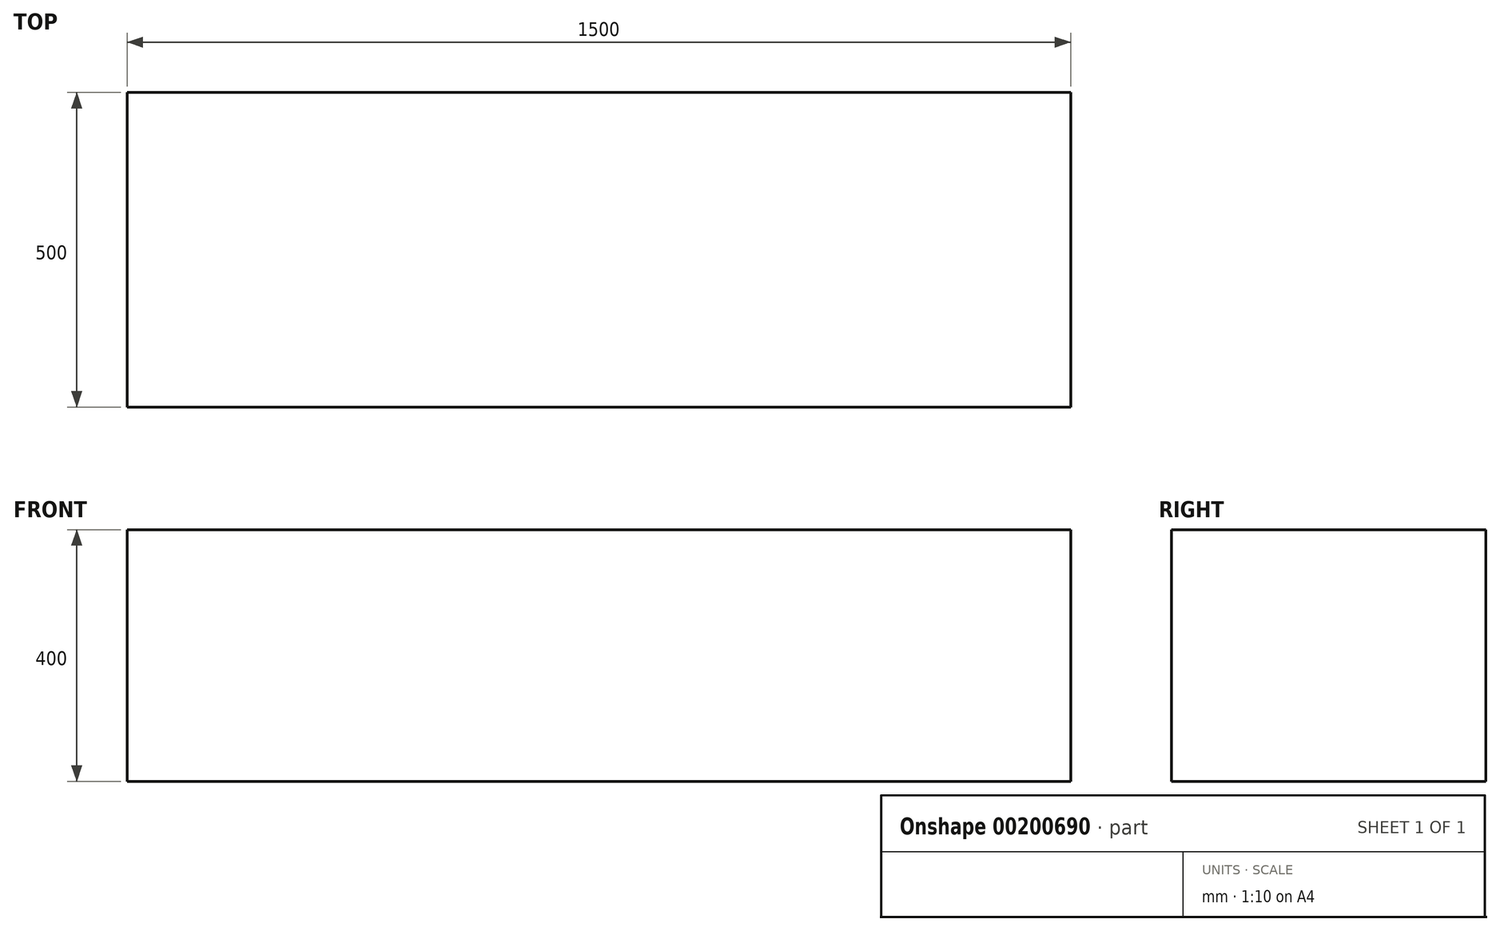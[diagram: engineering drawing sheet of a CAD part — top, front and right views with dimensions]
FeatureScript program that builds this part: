
annotation { "Feature Type Name" : "Feature", "Feature Type Description" : "" }
export const myFeature = defineFeature(function(context is Context, id is Id, definition is map)
    precondition{}
    {
        {
            var Q0;
            Q0=qCreatedBy(makeId("Front.planeOp"),FACE);
            var sketch = newSketch(context, id + "F0", { "sketchPlane" : qUnion([Q0])});
            skLineSegment(sketch, "E0.bottom", {"start": v(0, 0) * mm, "end": v(1500, 0) * mm});
            skLineSegment(sketch, "E0.top", {"start": v(0, 400) * mm, "end": v(1500, 400) * mm});
            skLineSegment(sketch, "E0.left", {"start": v(0, 0) * mm, "end": v(0, 400) * mm});
            skLineSegment(sketch, "E0.right", {"start": v(1500, 0) * mm, "end": v(1500, 400) * mm});
            skSolve(sketch);
        }
        {
            var Q0;
            Q0 = qSketchRegion(id + "F0", true);
            extrude(context, id + "F1", {"entities" : qUnion([Q0]), "depth" : 500 * mm});
        }
    });
